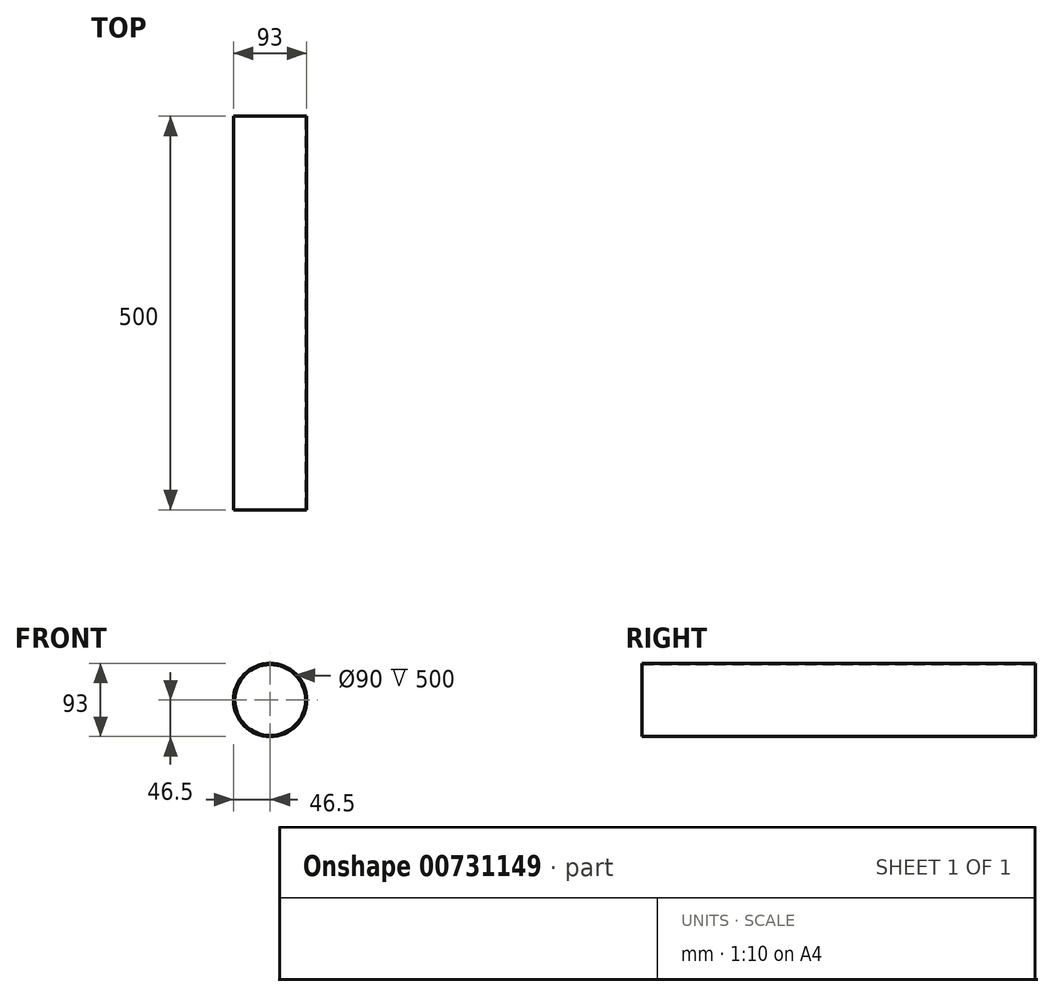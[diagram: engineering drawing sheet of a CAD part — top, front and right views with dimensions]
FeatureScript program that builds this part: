
annotation { "Feature Type Name" : "Feature", "Feature Type Description" : "" }
export const myFeature = defineFeature(function(context is Context, id is Id, definition is map)
    precondition{}
    {
        {
            var Q0;
            Q0=qCreatedBy(makeId("Front.planeOp"),FACE);
            var sketch = newSketch(context, id + "F0", { "sketchPlane" : qUnion([Q0])});
            skCircle(sketch, "E0", {"center": v(0, 0) * mm, "radius": 45 * mm});
            skCircle(sketch, "E1", {"center": v(0, 0) * mm, "radius": 46.5 * mm});
            skSolve(sketch);
        }
        {
            var Q0;
            Q0=qSketchRegion(id+"F0",true);
            extrude(context, id + "F1", {"entities" : qUnion([Q0]), "depth" : 500 * mm, "offsetDistance" : 25 * mm});
        }
    });
